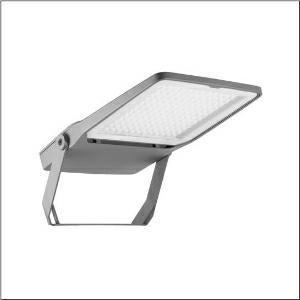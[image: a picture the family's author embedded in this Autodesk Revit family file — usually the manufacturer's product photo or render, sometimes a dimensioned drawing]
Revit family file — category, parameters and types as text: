
# Revit family: floodlight_fl_20_midi___rs17_5xa7682d2b1ac_83de
name_source: partatom
category: Lighting Fixtures
units: mm (PartAtom-declared; Revit-internal decimal feet)

## family parameters
Cut with Voids When Loaded = No
Host = Face
Light Source = No
Part Type = Normal
Room Calculation Point = No
Round Connector Dimension = Use Diameter
Shared = No

## types (1)
- --- (1 x LED 4000K / CRI = 70 (unbekannt), 19540 lm, 4000K)
    Apparent Load = 142 VA
    CIE Flux Codes = 79 92 99 100 100
    Color Rendering = 70
    Color Temperature = 4000K
    Default Elevation = 1800 mm
    Description = Floodlight FL 20 midi, floodlight, primary light control with lens, of plastic, primary optical cover: protective disc, of toughened safety glass, transparent, light distribution: RS17, light emission: direct distribution, primary light characteristic: rotationally symmetric, installation type: surface-mounted, LED High Power LED, rated luminous flux: 19.540 lm, light colour: 740, colour temperature: 4000K, control gear: ECG Plus, control: flexible luminous flux parameterisation, time-dependent luminous flux control, digital communication interface, power reduction, overheat protection, electronic power reduction, with terminal, 5-pole, max. 2.5mm², mains connection: 220..240V, AC, 50/60Hz, rated input power: 142W, LED unit, of diecast aluminium, powder-coated, Siteco® metallic grey (DB 702S), length: 654 mm, width: 450 mm, height: 76mm, housing frame, of diecast aluminium, powder-coated, Siteco® metallic grey (DB 702S), mounting bracket, of steel, powder-coated, Siteco® metallic grey (DB 702S), DALIprotection rating (complete): IP66, insulation class (complete): insulation class II (safety insulation), certification: CE, ENEC, VDE, protection symbol: D, permissible ambient temperature for indoor applications: -40..+40°C, permissible ambient temperature for outdoor applications: -40..+50°C, standard: DIN EN 12944, packaging unit: 1 piece

Light Distribution: RS17
    Height = 76 mm
    Lamp = 1 x LED 4000K / CRI >= 70 (unbekannt)
    Lamp Light Flux = 19540 lm
    Lamp count = 1
    Length = 672 mm
    Luminous efficacy = 138 lm/W
    Manufacturer = Siteco
    ModVariant = No
    Model = 5XA7682D2B1AC
    Number of Poles = 1
    OnlyDefault = Yes
    Power Factor = 1
    Product Name = Floodlight FL 20 midi | RS17
    Product group = floodlight | pylon top
    ProductGroupID = 6101
    Protection Class = Protection class II
    Protection Degree = IP 66
    RLX_Detail_Level = 1
    RlxData = <blob elided: 91897 chars, md5=f8c8d216>
    Socket = socket
    Standby Power = 0 W
    System Light Flux = 19540 lm
    System Power = 142 W
    Type Comments = factory setting: luminous flux: 100 % | dim-lin: 254 | 489 mA
    Type Image = l_1005943.jpg
    URL = http://relux.com
    VarID = @adj_142029
    Voltage = 0 V
    Weight = 0.00 kg
    Width = 450 mm

## geometry (parser evidence)
native form markers: Blend x4, Sweep x13
no freeform markers — native parametric forms only
